# Revit family: Hager-GOLF-Flush_mounted-IP40-With_Cover-With_DIN-Hosted-PL-pl
name_source: partatom
category: Electrical Equipment
units: mm (PartAtom-declared; Revit-internal decimal feet)

## family parameters
Cut with Voids When Loaded = No
Host = Face
Maintain Annotation Orientation = Yes
Panel Configuration = Two Columns, Circuits Across
Part Type = Panelboard
Room Calculation Point = No
Round Connector Dimension = Use Diameter
Shared = No

## types (25) — shared parameters
BC_MODEL_ID = 1539140
BC_OBJECT_ID = 512271
BC_OBJECT_VERSION = #12
Code hager = ADD-EC000214_EU
EF000003 - Sposób montażu = Montaż podtynkowy
EF000007 - Kolor = Biały
EF000024 - Odporność na promieniowanie UV = No
EF000049 - Głębokość = 97 mm  [stored 0.318241 ft]
EF000116 - Numer RAL = 9010
EF000218 - Głębokość wbudowania = 72 mm  [stored 0.23622 ft]
EF001062 - Wykonanie zgodne z Dyrektywą Kompatybilności Elektromagnetycznej EMC = No
EF001088 - Możliwość rozbudowy = Yes
EF001134 - Szyna DIN = Yes
EF004462 - Rodzaj zamknięcia = Inne
EF005474 - Stopień ochrony (IP) = IP40
EF006306 - Z zamkiem = No
EF015941 - Drzwi przepuszczające sygnał = Yes
ETIM class code = EC000214
ETIM class name = Small distribution board
HG000001-Number of columns-pl = 1
HG000002-with door or cover-pl = Yes
HG000003-Range-pl = GOLF
HG000005-Thickness-pl = 2 mm  [stored 0.00656168 ft]
HG000006-Flush mounted-pl = Yes
HG000009-Double swing door-pl = No
HG000010-Asymmetric doors-pl = No
HG000011-Empty rows from bottom-pl = No
HG000012-Door swing angle-pl = 90.00°
HG000013-Door on the left-pl = No
HG000014-Door on the right-pl = Yes
HG000015-Clearance visibility-pl = Yes
HG000016-Door 3D visibility-pl = Yes
HG000017-Distance between poles-pl = 18 mm  [stored 0.0590551 ft]
HG000060-RAL-number = 9010
HG000099-Onfly Template ID-pl-PL = 507532
Manufacturer = Hager
Name = Hager-GOLF-Flush_mounted-IP40-With_Cover-With_DIN-NoHosted-PL-pl
Name BIM&CO = Electricity
Name hager = ADD_Enclosures_EC000214
Uniformat = Low Tension Service & Dist.
Uniformat code = D501001
zero-valued in all types: Default Elevation, EF001131 - Głębokość wewnętrzna, HG000007-Number of empty columns-pl, HG000008-Number of empty rows-pl

## per-type parameters (varying)
| type | BC_VARIANT_ID | EF000008 - Szerokość | EF000040 - Wysokość | EF000118 - Z płytą montażową | EF000266 - Liczba rzędów | EF000332 - Wysokość wbudowania | EF000846 - Szerokość wbudowania | EF002950 - Szerokość wyrażona liczbą modułów | EF006244 - Transparentna pokrywa/drzwi | EF009212 - Wykonanie/rodzaj pokrywy | EF015776 - Listwa zaciskowa uziemienia | EF015777 - Listwa zaciskowa przewodu neutralnego | HG000004-Manufacturer reference-pl | HGEF000266-Liczba rzędów | HGEF0002950-Szerokość wyrażona liczbą modułów |
| GOLF-Flush_mounted_W204_H225_D97_4_Modular_Spacing-VF104PD | 1169382 | 204 mm | 225 mm  [stored 0.738189 ft] | No | 1 | 189 mm  [stored 0.620079 ft] | 170 mm  [stored 0.557743 ft] | 4 | No | Zamknięty | Yes | Yes | VF104PD | 1 | 4 |
| GOLF-Flush_mounted_W204_H225_D97_4_Modular_Spacing-VF104TD | 1169383 | 204 mm | 225 mm  [stored 0.738189 ft] | No | 1 | 189 mm  [stored 0.620079 ft] | 170 mm  [stored 0.557743 ft] | 4 | Yes | Zamknięty | Yes | Yes | VF104TD | 1 | 4 |
| GOLF-Flush_mounted_W275_H225_D97_8_Modular_Spacing-VF108PD | 1169384 | 275 mm | 225 mm  [stored 0.738189 ft] | No | 1 | 189 mm  [stored 0.620079 ft] | 242 mm  [stored 0.793963 ft] | 8 | No | Zamknięty | Yes | Yes | VF108PD | 1 | 8 |
| GOLF-Flush_mounted_W275_H225_D97_8_Modular_Spacing-VF108TD | 1169385 | 275 mm | 225 mm  [stored 0.738189 ft] | No | 1 | 189 mm  [stored 0.620079 ft] | 242 mm  [stored 0.793963 ft] | 8 | Yes | Zamknięty | Yes | Yes | VF108TD | 1 | 8 |
| GOLF-Flush_mounted_W352_H293_D97_12_Modular_Spacing-VF112PD | 1169386 | 352 mm  [stored 1.15486 ft] | 293 mm | No | 1 | 257 mm  [stored 0.843176 ft] | 318 mm  [stored 1.04331 ft] | 12 | No | Zamknięty | Yes | Yes | VF112PD | 1 | 12 |
| GOLF-Flush_mounted_W352_H293_D97_12_Modular_Spacing-VF112TD | 1169387 | 352 mm  [stored 1.15486 ft] | 293 mm | No | 1 | 257 mm  [stored 0.843176 ft] | 318 mm  [stored 1.04331 ft] | 12 | Yes | Zamknięty | Yes | Yes | VF112TD | 1 | 12 |
| GOLF-Flush_mounted_W460_H293_D97_18_Modular_Spacing-VF118PD | 1169388 | 460 mm  [stored 1.50919 ft] | 293 mm | No | 1 | 257 mm  [stored 0.843176 ft] | 426 mm  [stored 1.39764 ft] | 18 | No | Zamknięty | Yes | Yes | VF118PD | 1 | 18 |
| GOLF-Flush_mounted_W460_H293_D97_18_Modular_Spacing-VF118TD | 1169389 | 460 mm  [stored 1.50919 ft] | 293 mm | No | 1 | 257 mm  [stored 0.843176 ft] | 426 mm  [stored 1.39764 ft] | 18 | Yes | Zamknięty | Yes | Yes | VF118TD | 1 | 18 |
| GOLF-Flush_mounted_W532_H293_D97_22_Modular_Spacing-VF122PD | 1169390 | 532 mm  [stored 1.74541 ft] | 293 mm | No | 1 | 257 mm  [stored 0.843176 ft] | 498 mm  [stored 1.63386 ft] | 22 | No | Zamknięty | Yes | Yes | VF122PD | 1 | 22 |
| GOLF-Flush_mounted_W532_H293_D97_22_Modular_Spacing-VF122TD | 1169391 | 532 mm  [stored 1.74541 ft] | 293 mm | No | 1 | 257 mm  [stored 0.843176 ft] | 498 mm  [stored 1.63386 ft] | 22 | Yes | Zamknięty | Yes | Yes | VF122TD | 1 | 22 |
| GOLF-Flush_mounted_W382_H418_D97_12_Modular_Spacing-VF212PD | 1169392 | 382 mm  [stored 1.25328 ft] | 418 mm  [stored 1.37139 ft] | No | 2 | 382 mm  [stored 1.25328 ft] | 318 mm  [stored 1.04331 ft] | 12 | No | Zamknięty | Yes | Yes | VF212PD | 2 | 12 |
| GOLF-Flush_mounted_W382_H418_D97_12_Modular_Spacing-VF212TD | 1169393 | 382 mm  [stored 1.25328 ft] | 418 mm  [stored 1.37139 ft] | No | 2 | 382 mm  [stored 1.25328 ft] | 318 mm  [stored 1.04331 ft] | 12 | Yes | Zamknięty | Yes | Yes | VF212TD | 2 | 12 |
| GOLF-Flush_mounted_W460_H418_D97_18_Modular_Spacing-VF218PD | 1169394 | 460 mm  [stored 1.50919 ft] | 418 mm  [stored 1.37139 ft] | No | 2 | 382 mm  [stored 1.25328 ft] | 426 mm  [stored 1.39764 ft] | 18 | No | Zamknięty | Yes | Yes | VF218PD | 2 | 18 |
| GOLF-Flush_mounted_W460_H418_D97_18_Modular_Spacing-VF218PZF | 1169395 | 460 mm  [stored 1.50919 ft] | 418 mm  [stored 1.37139 ft] | Yes | 2 | 375 mm  [stored 1.23031 ft] | 426 mm  [stored 1.39764 ft] | 18 | No | Z otworem | No | No | VF218PZF | 2 | 18 |
| GOLF-Flush_mounted_W460_H418_D97_18_Modular_Spacing-VF218TD | 1169396 | 460 mm  [stored 1.50919 ft] | 418 mm  [stored 1.37139 ft] | No | 2 | 382 mm  [stored 1.25328 ft] | 426 mm  [stored 1.39764 ft] | 18 | Yes | Zamknięty | Yes | Yes | VF218TD | 2 | 18 |
| GOLF-Flush_mounted_W352_H543_D97_12_Modular_Spacing-VF312PD | 1169397 | 352 mm  [stored 1.15486 ft] | 543 mm  [stored 1.7815 ft] | No | 3 | 507 mm  [stored 1.66339 ft] | 318 mm  [stored 1.04331 ft] | 12 | No | Zamknięty | Yes | Yes | VF312PD | 3 | 12 |
| GOLF-Flush_mounted_W352_H543_D97_12_Modular_Spacing-VF312TD | 1169398 | 352 mm  [stored 1.15486 ft] | 543 mm  [stored 1.7815 ft] | No | 3 | 507 mm  [stored 1.66339 ft] | 318 mm  [stored 1.04331 ft] | 12 | Yes | Zamknięty | Yes | Yes | VF312TD | 3 | 12 |
| GOLF-Flush_mounted_W460_H543_D97_18_Modular_Spacing-VF318PD | 1169399 | 460 mm  [stored 1.50919 ft] | 543 mm  [stored 1.7815 ft] | No | 3 | 507 mm  [stored 1.66339 ft] | 426 mm  [stored 1.39764 ft] | 18 | No | Zamknięty | Yes | Yes | VF318PD | 3 | 18 |
| GOLF-Flush_mounted_W460_H543_D97_18_Modular_Spacing-VF318PZF | 1169400 | 460 mm  [stored 1.50919 ft] | 543 mm  [stored 1.7815 ft] | Yes | 3 | 495 mm  [stored 1.62402 ft] | 426 mm  [stored 1.39764 ft] | 18 | No | Z otworem | No | No | VF318PZF | 3 | 18 |
| GOLF-Flush_mounted_W460_H543_D97_18_Modular_Spacing-VF318TD | 1169401 | 460 mm  [stored 1.50919 ft] | 543 mm  [stored 1.7815 ft] | No | 3 | 507 mm  [stored 1.66339 ft] | 426 mm  [stored 1.39764 ft] | 18 | Yes | Zamknięty | Yes | Yes | VF318TD | 3 | 18 |
| GOLF-Flush_mounted_W352_H688_D97_12_Modular_Spacing-VF412PD | 1169402 | 352 mm  [stored 1.15486 ft] | 688 mm  [stored 2.25722 ft] | No | 4 | 652 mm  [stored 2.13911 ft] | 318 mm  [stored 1.04331 ft] | 12 | No | Zamknięty | Yes | Yes | VF412PD | 4 | 12 |
| GOLF-Flush_mounted_W352_H688_D97_12_Modular_Spacing-VF412TD | 1169403 | 352 mm  [stored 1.15486 ft] | 688 mm  [stored 2.25722 ft] | No | 4 | 652 mm  [stored 2.13911 ft] | 318 mm  [stored 1.04331 ft] | 12 | Yes | Zamknięty | Yes | Yes | VF412TD | 4 | 12 |
| GOLF-Flush_mounted_W460_H688_D97_18_Modular_Spacing-VF418PD | 1169404 | 460 mm  [stored 1.50919 ft] | 688 mm  [stored 2.25722 ft] | No | 4 | 652 mm  [stored 2.13911 ft] | 426 mm  [stored 1.39764 ft] | 18 | No | Zamknięty | Yes | Yes | VF418PD | 4 | 18 |
| GOLF-Flush_mounted_W460_H688_D97_18_Modular_Spacing-VF418PZF | 1169405 | 460 mm  [stored 1.50919 ft] | 688 mm  [stored 2.25722 ft] | Yes | 4 | 640 mm  [stored 2.09974 ft] | 426 mm  [stored 1.39764 ft] | 18 | No | Z otworem | No | No | VF418PZF | 4 | 18 |
| GOLF-Flush_mounted_W460_H688_D97_18_Modular_Spacing-VF418TD | 1169406 | 460 mm  [stored 1.50919 ft] | 688 mm  [stored 2.25722 ft] | No | 4 | 652 mm  [stored 2.13911 ft] | 426 mm  [stored 1.39764 ft] | 18 | Yes | Zamknięty | Yes | Yes | VF418TD | 4 | 18 |

note: column(s) folded — value = type name in every type: Reference

note: [stored X ft] marks values corroborated as IEEE doubles in the binary element streams (Revit-internal decimal feet)

## geometry (parser evidence)
native form markers: Sweep x14
no freeform markers — native parametric forms only
